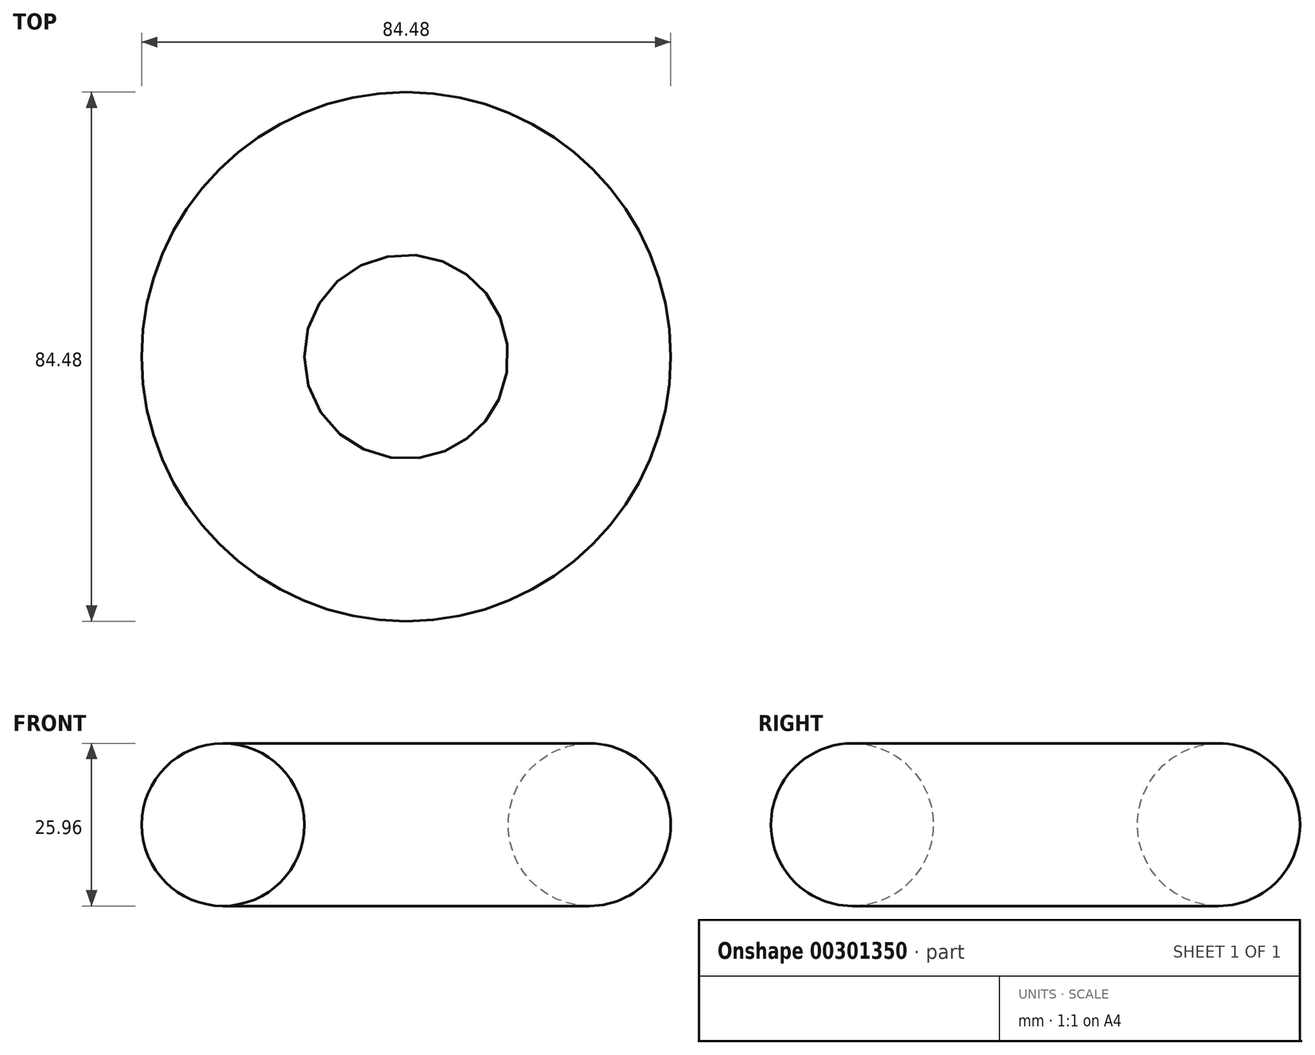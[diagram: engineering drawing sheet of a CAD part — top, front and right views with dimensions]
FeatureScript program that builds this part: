
annotation { "Feature Type Name" : "Feature", "Feature Type Description" : "" }
export const myFeature = defineFeature(function(context is Context, id is Id, definition is map)
    precondition{}
    {
        {
            var Q0;
            Q0=qCreatedBy(makeId("Front.planeOp"),FACE);
            var sketch = newSketch(context, id + "F0", { "sketchPlane" : qUnion([Q0])});
            skLineSegment(sketch, "E0", {"start": v(0, 0) * mm, "end": v(0, 73.82) * mm});
            skCircle(sketch, "E1", {"center": v(29.26, 32.77) * mm, "radius": 12.98 * mm});
            skSolve(sketch);
        }
        {
            var Q0;
            Q0=makeQuery(id+"F0.imprint","IMPRINT",FACE,{"disambiguationData":[TD([[makeQuery(id+"F0.imprint","IMPRINT",EDGE,{"derivedFrom":sQuery(id+"F0.wireOp",EDGE,"E1")}),1.0]])]});
            var Q1;
            Q1=sQuery(id+"F0.wireOp",EDGE,"E0");
            revolve(context, id + "F1", {"entities" : qUnion([Q0]), "axis" : qUnion([Q1]), "revolveType" : RevolveType.FULL});
        }
    });
